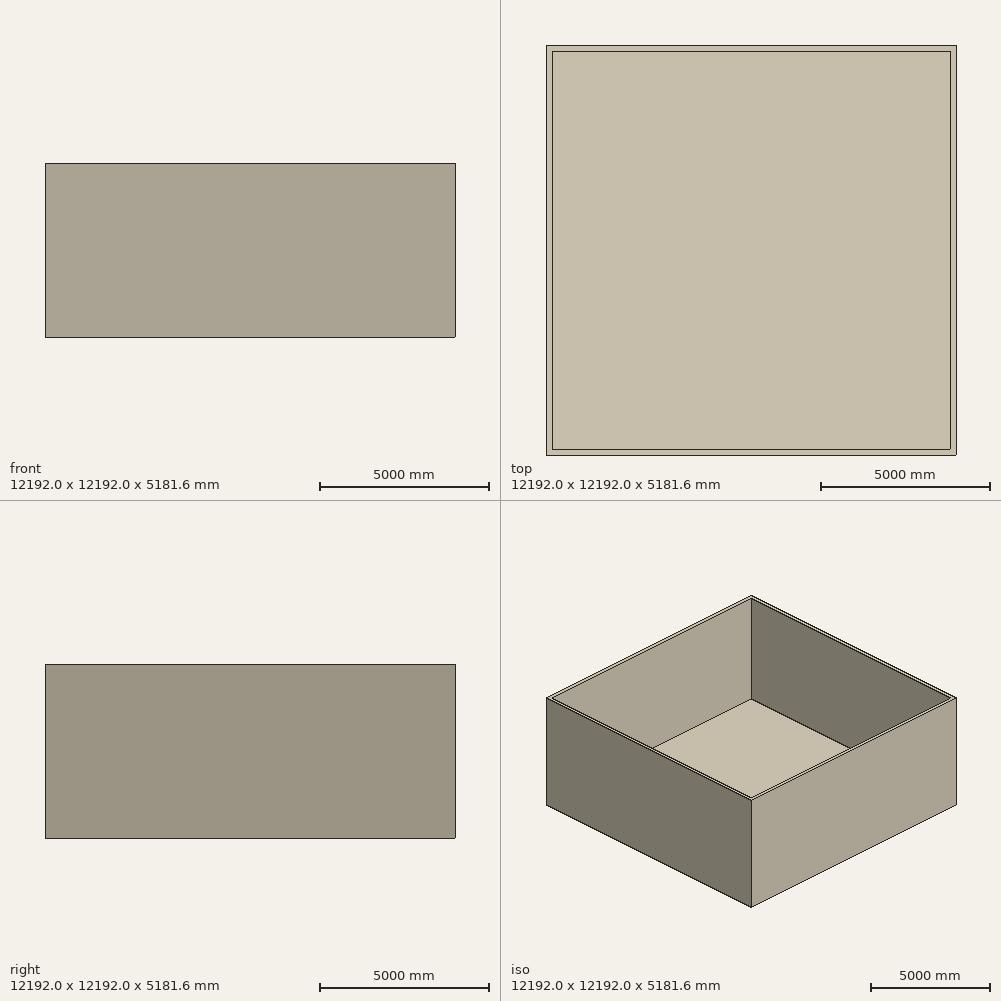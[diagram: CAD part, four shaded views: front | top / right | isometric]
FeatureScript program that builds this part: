
annotation { "Feature Type Name" : "Feature", "Feature Type Description" : "" }
export const myFeature = defineFeature(function(context is Context, id is Id, definition is map)
    precondition{}
    {
        {
            var Q0;
            Q0=qCreatedBy(makeId("Top.planeOp"),FACE);
            var sketch = newSketch(context, id + "F0", { "sketchPlane" : qUnion([Q0])});
            skLineSegment(sketch, "E0.bottom", {"start": v(0, 12192) * mm, "end": v(12192, 12192) * mm});
            skLineSegment(sketch, "E0.top", {"start": v(0, 0) * mm, "end": v(12192, 0) * mm});
            skLineSegment(sketch, "E0.left", {"start": v(0, 12192) * mm, "end": v(0, 0) * mm});
            skLineSegment(sketch, "E0.right", {"start": v(12192, 12192) * mm, "end": v(12192, 0) * mm});
            skSolve(sketch);
        }
        {
            var Q0;
            Q0=makeQuery(id+"F0.imprint","IMPRINT",FACE,{"disambiguationData":[TD([[makeQuery(id+"F0.imprint","IMPRINT",EDGE,{"derivedFrom":sQuery(id+"F0.wireOp",EDGE,"E0.bottom")}),-1.0]])]});
            extrude(context, id + "F1", {"entities" : qUnion([Q0]), "depth" : 304.8 * mm});
        }
        {
            var Q0;
            Q0=makeQuery(id+"F1.opExtrude","CAP_FACE",FACE,{"disambiguationData":[OSD([sQuery(id+"F0.wireOp",EDGE,"E0.bottom"),sQuery(id+"F0.wireOp",EDGE,"E0.top"),sQuery(id+"F0.wireOp",EDGE,"E0.left"),sQuery(id+"F0.wireOp",EDGE,"E0.right")])],"isStart":false});
            var sketch = newSketch(context, id + "F2", { "sketchPlane" : qUnion([Q0])});
            skLineSegment(sketch, "E1.0", {"start": v(0, 0) * mm, "end": v(12192, 0) * mm});
            skLineSegment(sketch, "E2.0", {"start": v(12192, 12192) * mm, "end": v(12192, 0) * mm});
            skLineSegment(sketch, "E3.0", {"start": v(0, 12192) * mm, "end": v(0, 0) * mm});
            skLineSegment(sketch, "E4.0", {"start": v(0, 12192) * mm, "end": v(12192, 12192) * mm});
            skLineSegment(sketch, "E5.0", {"start": v(165.1, 12026.9) * mm, "end": v(165.1, 165.1) * mm});
            skLineSegment(sketch, "E5.1", {"start": v(165.1, 12026.9) * mm, "end": v(12026.9, 12026.9) * mm});
            skLineSegment(sketch, "E5.2", {"start": v(12026.9, 12026.9) * mm, "end": v(12026.9, 165.1) * mm});
            skLineSegment(sketch, "E5.3", {"start": v(165.1, 165.1) * mm, "end": v(12026.9, 165.1) * mm});
            skSolve(sketch);
        }
        {
            var Q0;
            Q0=qSketchRegion(id+"F2",true);
            extrude(context, id + "F3", {"entities" : qUnion([Q0]), "operationType" : NewBodyOperationType.ADD, "depth" : 4876.8 * mm});
        }
    });
